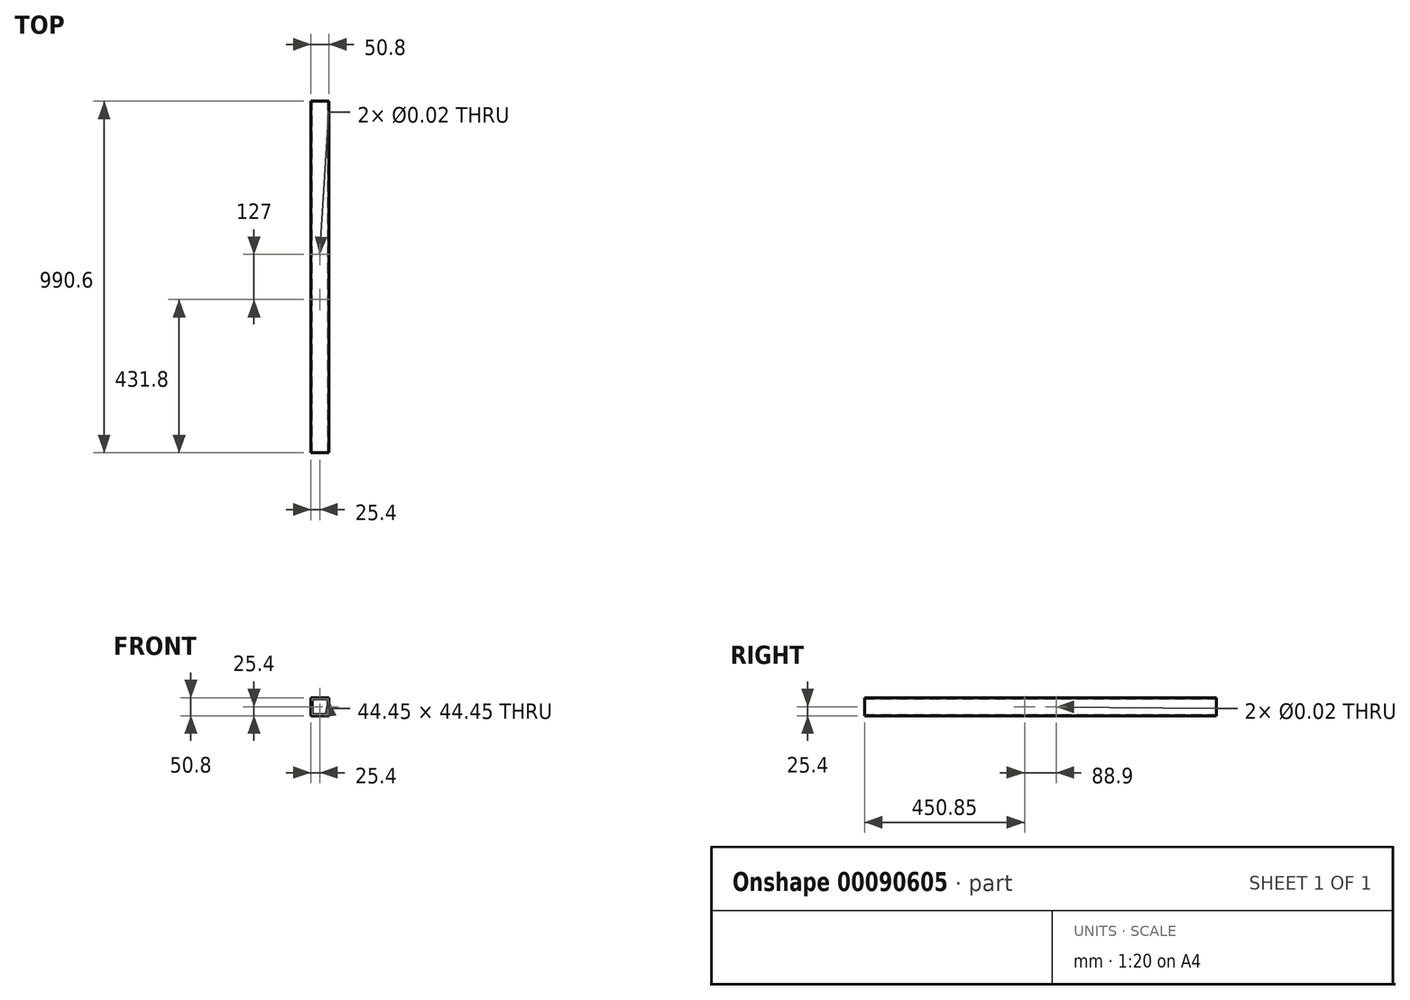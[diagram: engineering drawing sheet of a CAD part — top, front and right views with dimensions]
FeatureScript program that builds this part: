
annotation { "Feature Type Name" : "Feature", "Feature Type Description" : "" }
export const myFeature = defineFeature(function(context is Context, id is Id, definition is map)
    precondition{}
    {
        {
            var Q0;
            Q0=qCreatedBy(makeId("Front.planeOp"),FACE);
            var sketch = newSketch(context, id + "F0", { "sketchPlane" : qUnion([Q0])});
            skLineSegment(sketch, "E0.bottom", {"start": v(25.4, 25.4) * mm, "end": v(-25.4, 25.4) * mm});
            skLineSegment(sketch, "E0.top", {"start": v(25.4, -25.4) * mm, "end": v(-25.4, -25.4) * mm});
            skLineSegment(sketch, "E0.left", {"start": v(25.4, 25.4) * mm, "end": v(25.4, -25.4) * mm});
            skLineSegment(sketch, "E0.right", {"start": v(-25.4, 25.4) * mm, "end": v(-25.4, -25.4) * mm});
            skPoint(sketch, "E0.middle", {"position": v(0, 0) * mm});
            skLineSegment(sketch, "E1.bottom", {"start": v(22.23, 22.23) * mm, "end": v(-22.23, 22.23) * mm});
            skLineSegment(sketch, "E1.top", {"start": v(22.23, -22.23) * mm, "end": v(-22.23, -22.23) * mm});
            skLineSegment(sketch, "E1.left", {"start": v(22.23, 22.23) * mm, "end": v(22.23, -22.23) * mm});
            skLineSegment(sketch, "E1.right", {"start": v(-22.23, 22.23) * mm, "end": v(-22.23, -22.23) * mm});
            skSolve(sketch);
        }
        {
            var Q0;
            Q0=makeQuery(id+"F0.imprint","IMPRINT",FACE,{"disambiguationData":[TD([[makeQuery(id+"F0.imprint","IMPRINT",EDGE,{"derivedFrom":sQuery(id+"F0.wireOp",EDGE,"E0.bottom")}),1.0]])]});
            extrude(context, id + "F1", {"entities" : qUnion([Q0]), "endBound" : BoundingType.SYMMETRIC, "depth" : 990.6 * mm});
        }
        {
            var Q0;
            Q0=makeQuery(id+"F1.opExtrude","SWEPT_FACE",FACE,{"disambiguationData":[OSD([sQuery(id+"F0.wireOp",EDGE,"E0.bottom")])]});
            var sketch = newSketch(context, id + "F2", { "sketchPlane" : qUnion([Q0])});
            skPoint(sketch, "E2", {"position": v(0, -63.5) * mm});
            skPoint(sketch, "E3", {"position": v(0, 63.5) * mm});
            skSolve(sketch);
        }
        {
            var Q0;
            Q0=sQuery(id+"F2.wireOp",VERTEX,"E3");
            var Q1;
            Q1=sQuery(id+"F2.wireOp",VERTEX,"E2");
            var Q2;
            Q2=makeQuery(id+"F1.opExtrude","SWEPT_BODY",BODY,{"disambiguationData":[OSD([sQuery(id+"F0.wireOp",EDGE,"E0.bottom"),sQuery(id+"F0.wireOp",EDGE,"E0.top"),sQuery(id+"F0.wireOp",EDGE,"E0.left"),sQuery(id+"F0.wireOp",EDGE,"E0.right"),sQuery(id+"F0.wireOp",EDGE,"E1.bottom"),sQuery(id+"F0.wireOp",EDGE,"E1.top"),sQuery(id+"F0.wireOp",EDGE,"E1.left"),sQuery(id+"F0.wireOp",EDGE,"E1.right")])]});
            hole(context, id + "F3", {"style" : HoleStyle.SIMPLE, "endStyle" : HoleEndStyle.BLIND, "standardTappedOrClearance" : lookupTablePath({ "standard" : "ANSI", "size" : "1/2 (0.5)", "type" : "Drilled" }), "standardBlindInLast" : lookupTablePath({ "standard" : "ANSI", "size" : "1/2", "type" : "Drilled" }), "holeDiameter" : 1 / 50.8 * mm, "holeDepth" : 12.7 * mm, "startFromSketch" : true, "locations" : qUnion([Q0, Q1]), "scope" : qUnion([Q2])});
        }
        {
            var Q0;
            Q0=makeQuery(id+"F1.opExtrude","SWEPT_FACE",FACE,{"disambiguationData":[OSD([sQuery(id+"F0.wireOp",EDGE,"E0.left")])]});
            var sketch = newSketch(context, id + "F4", { "sketchPlane" : qUnion([Q0])});
            skPoint(sketch, "E4", {"position": v(-44.45, 0) * mm});
            skPoint(sketch, "E5", {"position": v(44.45, 0) * mm});
            skSolve(sketch);
        }
        {
            var Q0;
            Q0=sQuery(id+"F4.wireOp",VERTEX,"E5");
            var Q1;
            Q1=sQuery(id+"F4.wireOp",VERTEX,"E4");
            var Q2;
            Q2=makeQuery(id+"F1.opExtrude","SWEPT_BODY",BODY,{"disambiguationData":[OSD([sQuery(id+"F0.wireOp",EDGE,"E0.bottom"),sQuery(id+"F0.wireOp",EDGE,"E0.top"),sQuery(id+"F0.wireOp",EDGE,"E0.left"),sQuery(id+"F0.wireOp",EDGE,"E0.right"),sQuery(id+"F0.wireOp",EDGE,"E1.bottom"),sQuery(id+"F0.wireOp",EDGE,"E1.top"),sQuery(id+"F0.wireOp",EDGE,"E1.left"),sQuery(id+"F0.wireOp",EDGE,"E1.right")])]});
            hole(context, id + "F5", {"style" : HoleStyle.SIMPLE, "endStyle" : HoleEndStyle.BLIND, "standardTappedOrClearance" : lookupTablePath({ "standard" : "ANSI", "size" : "1/2 (0.5)", "type" : "Drilled" }), "standardBlindInLast" : lookupTablePath({ "standard" : "ANSI", "size" : "1/2", "type" : "Drilled" }), "holeDiameter" : 1 / 50.8 * mm, "holeDepth" : 12.7 * mm, "startFromSketch" : true, "locations" : qUnion([Q0, Q1]), "scope" : qUnion([Q2])});
        }
    });
